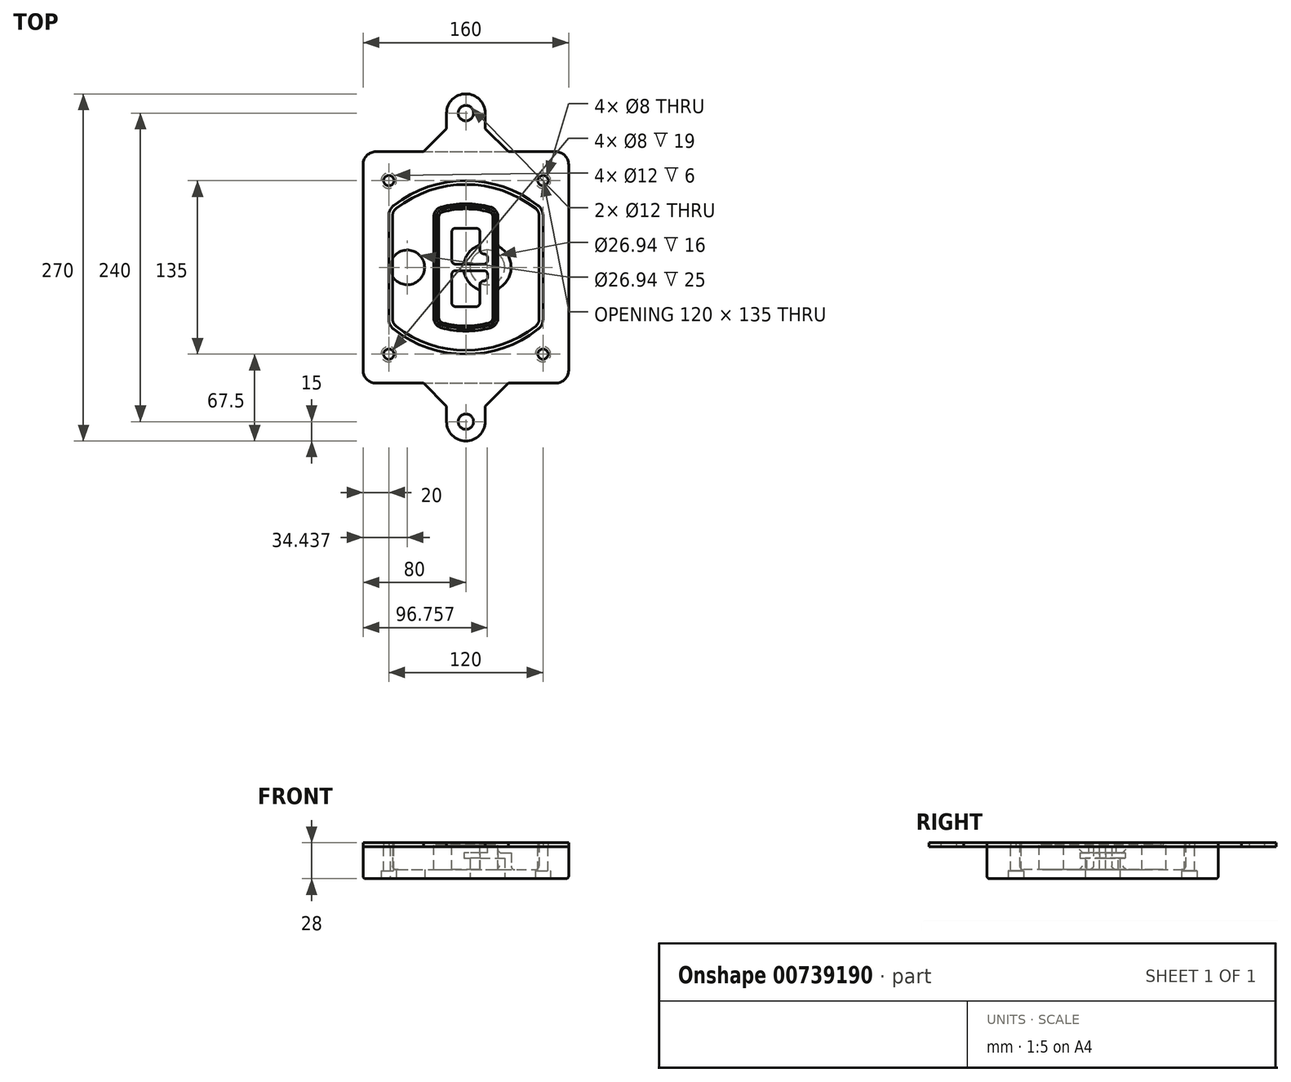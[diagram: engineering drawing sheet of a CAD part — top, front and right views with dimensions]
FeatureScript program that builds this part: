
annotation { "Feature Type Name" : "Feature", "Feature Type Description" : "" }
export const myFeature = defineFeature(function(context is Context, id is Id, definition is map)
    precondition{}
    {
        {
            var Q0;
            Q0=qCreatedBy(makeId("Top.planeOp"),FACE);
            var sketch = newSketch(context, id + "F0", { "sketchPlane" : qUnion([Q0])});
            skPoint(sketch, "E0.rect.middle", {"position": v(0, 0) * mm});
            skLineSegment(sketch, "E1.bottom", {"start": v(-70, -90) * mm, "end": v(70, -90) * mm});
            skLineSegment(sketch, "E1.top", {"start": v(-70, 90) * mm, "end": v(70, 90) * mm});
            skLineSegment(sketch, "E1.left", {"start": v(-80, -80) * mm, "end": v(-80, 80) * mm});
            skLineSegment(sketch, "E1.right", {"start": v(80, -80) * mm, "end": v(80, 80) * mm});
            skLineSegment(sketch, "E2", {"start": v(-80, 90) * mm, "end": v(80, -90) * mm, "construction": true});
            skLineSegment(sketch, "E3", {"start": v(80, 90) * mm, "end": v(-80, -90) * mm, "construction": true});
            skCircle(sketch, "E4", {"center": v(-60, 67.5) * mm, "radius": 4 * mm});
            skCircle(sketch, "E5", {"center": v(60, 67.5) * mm, "radius": 4 * mm});
            skCircle(sketch, "E6", {"center": v(60, -67.5) * mm, "radius": 4 * mm});
            skCircle(sketch, "E7", {"center": v(-60, -67.5) * mm, "radius": 4 * mm});
            skLineSegment(sketch, "E8", {"start": v(-60, 67.5) * mm, "end": v(60, 67.5) * mm, "construction": true});
            skLineSegment(sketch, "E9", {"start": v(60, 67.5) * mm, "end": v(60, -67.5) * mm, "construction": true});
            skLineSegment(sketch, "E10", {"start": v(60, -67.5) * mm, "end": v(-60, -67.5) * mm, "construction": true});
            skLineSegment(sketch, "E11", {"start": v(-60, -67.5) * mm, "end": v(-60, 67.5) * mm, "construction": true});
            skLineSegment(sketch, "E12", {"start": v(-60, 40.3) * mm, "end": v(-60, -40.3) * mm});
            skLineSegment(sketch, "E13", {"start": v(60, 40.3) * mm, "end": v(60, -40.3) * mm});
            skArc(sketch, "E14", {"start": v(56.15, 48.18) * mm, "mid": v(0, 67.5) * mm, "end": v(-56.15, 48.18) * mm});
            skArc(sketch, "E15", {"start": v(-56.15, -48.18) * mm, "mid": v(0, -67.5) * mm, "end": v(56.15, -48.18) * mm});
            skLineSegment(sketch, "E16", {"start": v(-60, 0) * mm, "end": v(60, 0) * mm, "construction": true});
            skPoint(sketch, "E17.visualSharp", {"position": v(-60, -45) * mm});
            skArc(sketch, "E17.filletArc", {"start": v(-60, -40.3) * mm, "mid": v(-58.99, -44.68) * mm, "end": v(-56.15, -48.18) * mm});
            skPoint(sketch, "E18.visualSharp", {"position": v(-60, 45) * mm});
            skArc(sketch, "E18.filletArc", {"start": v(-56.15, 48.18) * mm, "mid": v(-58.99, 44.68) * mm, "end": v(-60, 40.3) * mm});
            skPoint(sketch, "E19.visualSharp", {"position": v(60, 45) * mm});
            skArc(sketch, "E19.filletArc", {"start": v(60, 40.3) * mm, "mid": v(58.99, 44.68) * mm, "end": v(56.15, 48.18) * mm});
            skPoint(sketch, "E20.visualSharp", {"position": v(60, -45) * mm});
            skArc(sketch, "E20.filletArc", {"start": v(56.15, -48.18) * mm, "mid": v(58.99, -44.68) * mm, "end": v(60, -40.3) * mm});
            skPoint(sketch, "E21.visualSharp", {"position": v(-80, 90) * mm});
            skArc(sketch, "E21.filletArc", {"start": v(-70, 90) * mm, "mid": v(-77.07, 87.07) * mm, "end": v(-80, 80) * mm});
            skPoint(sketch, "E22.visualSharp", {"position": v(80, 90) * mm});
            skArc(sketch, "E22.filletArc", {"start": v(80, 80) * mm, "mid": v(77.07, 87.07) * mm, "end": v(70, 90) * mm});
            skPoint(sketch, "E23.visualSharp", {"position": v(80, -90) * mm});
            skArc(sketch, "E23.filletArc", {"start": v(70, -90) * mm, "mid": v(77.07, -87.07) * mm, "end": v(80, -80) * mm});
            skPoint(sketch, "E24.visualSharp", {"position": v(-80, -90) * mm});
            skArc(sketch, "E24.filletArc", {"start": v(-80, -80) * mm, "mid": v(-77.07, -87.07) * mm, "end": v(-70, -90) * mm});
            skArc(sketch, "E25.0", {"start": v(57, 40.3) * mm, "mid": v(56.3, 43.36) * mm, "end": v(54.3, 45.81) * mm});
            skLineSegment(sketch, "E25.1", {"start": v(57, 40.3) * mm, "end": v(57, -40.3) * mm});
            skArc(sketch, "E25.2", {"start": v(54.3, -45.81) * mm, "mid": v(56.3, -43.36) * mm, "end": v(57, -40.3) * mm});
            skArc(sketch, "E25.3", {"start": v(-54.3, -45.81) * mm, "mid": v(0, -64.5) * mm, "end": v(54.3, -45.81) * mm});
            skArc(sketch, "E25.4", {"start": v(-57, -40.3) * mm, "mid": v(-56.3, -43.36) * mm, "end": v(-54.3, -45.81) * mm});
            skArc(sketch, "E25.5", {"start": v(54.3, 45.81) * mm, "mid": v(0, 64.5) * mm, "end": v(-54.3, 45.81) * mm});
            skLineSegment(sketch, "E25.6", {"start": v(-57, 40.3) * mm, "end": v(-57, -40.3) * mm});
            skArc(sketch, "E25.7", {"start": v(-54.3, 45.81) * mm, "mid": v(-56.3, 43.36) * mm, "end": v(-57, 40.3) * mm});
            skArc(sketch, "E26.0", {"start": v(-58.62, 51.33) * mm, "mid": v(-62.58, 46.43) * mm, "end": v(-64, 40.3) * mm});
            skArc(sketch, "E26.1", {"start": v(58.62, 51.33) * mm, "mid": v(0, 71.5) * mm, "end": v(-58.62, 51.33) * mm});
            skArc(sketch, "E26.2", {"start": v(64, 40.3) * mm, "mid": v(62.58, 46.43) * mm, "end": v(58.62, 51.33) * mm});
            skLineSegment(sketch, "E26.3", {"start": v(64, 40.3) * mm, "end": v(64, -40.3) * mm});
            skArc(sketch, "E26.4", {"start": v(58.62, -51.33) * mm, "mid": v(62.58, -46.43) * mm, "end": v(64, -40.3) * mm});
            skLineSegment(sketch, "E26.5", {"start": v(-64, 40.3) * mm, "end": v(-64, -40.3) * mm});
            skArc(sketch, "E26.6", {"start": v(-58.62, -51.33) * mm, "mid": v(0, -71.5) * mm, "end": v(58.62, -51.33) * mm});
            skArc(sketch, "E26.7", {"start": v(-64, -40.3) * mm, "mid": v(-62.58, -46.43) * mm, "end": v(-58.62, -51.33) * mm});
            skSolve(sketch);
        }
        {
            var Q0;
            Q0=makeQuery(id+"F0.imprint","IMPRINT",FACE,{"disambiguationData":[TD([[makeQuery(id+"F0.imprint","IMPRINT",EDGE,{"derivedFrom":sQuery(id+"F0.wireOp",EDGE,"E1.bottom")}),1.0]])]});
            var Q1;
            Q1=makeQuery(id+"F0.imprint","IMPRINT",FACE,{"disambiguationData":[TD([[makeQuery(id+"F0.imprint","IMPRINT",EDGE,{"derivedFrom":sQuery(id+"F0.wireOp",EDGE,"E12")}),1.0]])]});
            var Q2;
            Q2=makeQuery(id+"F0.imprint","IMPRINT",FACE,{"disambiguationData":[TD([[makeQuery(id+"F0.imprint","IMPRINT",EDGE,{"derivedFrom":sQuery(id+"F0.wireOp",EDGE,"E25.0")}),1.0]])]});
            var Q3;
            Q3=makeQuery(id+"F0.imprint","IMPRINT",FACE,{"disambiguationData":[TD([[makeQuery(id+"F0.imprint","IMPRINT",EDGE,{"derivedFrom":sQuery(id+"F0.wireOp",EDGE,"E12")}),-1.0]])]});
            extrude(context, id + "F1", {"entities" : qUnion([Q0, Q1, Q2, Q3]), "oppositeDirection" : true, "depth" : 25 * mm});
        }
        {
            var Q0;
            Q0=makeQuery(id+"F0.imprint","IMPRINT",FACE,{"disambiguationData":[TD([[makeQuery(id+"F0.imprint","IMPRINT",EDGE,{"derivedFrom":sQuery(id+"F0.wireOp",EDGE,"E12")}),1.0]])]});
            extrude(context, id + "F2", {"entities" : qUnion([Q0]), "operationType" : NewBodyOperationType.ADD, "depth" : 3 * mm});
        }
        {
            var Q0;
            Q0=makeQuery(id+"F0.imprint","IMPRINT",FACE,{"disambiguationData":[TD([[makeQuery(id+"F0.imprint","IMPRINT",EDGE,{"derivedFrom":sQuery(id+"F0.wireOp",EDGE,"E25.0")}),1.0]])]});
            extrude(context, id + "F3", {"entities" : qUnion([Q0]), "operationType" : NewBodyOperationType.REMOVE, "oppositeDirection" : true, "depth" : 18 * mm});
        }
        {
            var Q0;
            Q0=makeQuery(id+"F2.opExtrude","CAP_FACE",FACE,{"disambiguationData":[OSD([sQuery(id+"F0.wireOp",EDGE,"E12"),sQuery(id+"F0.wireOp",EDGE,"E13"),sQuery(id+"F0.wireOp",EDGE,"E14"),sQuery(id+"F0.wireOp",EDGE,"E15"),sQuery(id+"F0.wireOp",EDGE,"E17.filletArc"),sQuery(id+"F0.wireOp",EDGE,"E18.filletArc"),sQuery(id+"F0.wireOp",EDGE,"E19.filletArc"),sQuery(id+"F0.wireOp",EDGE,"E20.filletArc"),sQuery(id+"F0.wireOp",EDGE,"E25.0"),sQuery(id+"F0.wireOp",EDGE,"E25.1"),sQuery(id+"F0.wireOp",EDGE,"E25.2"),sQuery(id+"F0.wireOp",EDGE,"E25.3"),sQuery(id+"F0.wireOp",EDGE,"E25.4"),sQuery(id+"F0.wireOp",EDGE,"E25.5"),sQuery(id+"F0.wireOp",EDGE,"E25.6"),sQuery(id+"F0.wireOp",EDGE,"E25.7")])],"isStart":false});
            var sketch = newSketch(context, id + "F4", { "sketchPlane" : qUnion([Q0])});
            skArc(sketch, "E27.0", {"start": v(-19.08, -46.97) * mm, "mid": v(0, -49.5) * mm, "end": v(19.08, -46.97) * mm});
            skArc(sketch, "E28.0", {"start": v(19.08, 46.97) * mm, "mid": v(0, 49.5) * mm, "end": v(-19.08, 46.97) * mm});
            skLineSegment(sketch, "E29", {"start": v(-25, 39.25) * mm, "end": v(-25, -39.25) * mm});
            skLineSegment(sketch, "E30", {"start": v(25, 39.25) * mm, "end": v(25, -39.25) * mm});
            skLineSegment(sketch, "E31", {"start": v(-25, 45.1) * mm, "end": v(25, 45.1) * mm, "construction": true});
            skLineSegment(sketch, "E32", {"start": v(-25, -45.1) * mm, "end": v(25, -45.1) * mm, "construction": true});
            skPoint(sketch, "E33.visualSharp", {"position": v(-25, 45.1) * mm});
            skArc(sketch, "E33.filletArc", {"start": v(-19.08, 46.97) * mm, "mid": v(-23.35, 44.11) * mm, "end": v(-25, 39.25) * mm});
            skPoint(sketch, "E34.visualSharp", {"position": v(25, 45.1) * mm});
            skArc(sketch, "E34.filletArc", {"start": v(25, 39.25) * mm, "mid": v(23.35, 44.11) * mm, "end": v(19.08, 46.97) * mm});
            skPoint(sketch, "E35.visualSharp", {"position": v(25, -45.1) * mm});
            skArc(sketch, "E35.filletArc", {"start": v(19.08, -46.97) * mm, "mid": v(23.35, -44.11) * mm, "end": v(25, -39.25) * mm});
            skPoint(sketch, "E36.visualSharp", {"position": v(-25, -45.1) * mm});
            skArc(sketch, "E36.filletArc", {"start": v(-25, -39.25) * mm, "mid": v(-23.35, -44.11) * mm, "end": v(-19.08, -46.97) * mm});
            skArc(sketch, "E37.0", {"start": v(54.3, 45.81) * mm, "mid": v(0, 64.5) * mm, "end": v(-54.3, 45.81) * mm});
            skArc(sketch, "E37.1", {"start": v(-54.3, 45.81) * mm, "mid": v(-56.3, 43.36) * mm, "end": v(-57, 40.3) * mm});
            skLineSegment(sketch, "E37.2", {"start": v(-57, 40.3) * mm, "end": v(-57, -40.3) * mm});
            skArc(sketch, "E37.3", {"start": v(-57, -40.3) * mm, "mid": v(-56.3, -43.36) * mm, "end": v(-54.3, -45.81) * mm});
            skArc(sketch, "E37.4", {"start": v(-54.3, -45.81) * mm, "mid": v(0, -64.5) * mm, "end": v(54.3, -45.81) * mm});
            skArc(sketch, "E37.5", {"start": v(54.3, -45.81) * mm, "mid": v(56.3, -43.36) * mm, "end": v(57, -40.3) * mm});
            skLineSegment(sketch, "E37.6", {"start": v(57, 40.3) * mm, "end": v(57, -40.3) * mm});
            skArc(sketch, "E37.7", {"start": v(57, 40.3) * mm, "mid": v(56.3, 43.36) * mm, "end": v(54.3, 45.81) * mm});
            skLineSegment(sketch, "E38.0", {"start": v(23, 39.25) * mm, "end": v(23, -39.25) * mm});
            skArc(sketch, "E38.1", {"start": v(18.56, -45.04) * mm, "mid": v(21.76, -42.9) * mm, "end": v(23, -39.25) * mm});
            skArc(sketch, "E38.2", {"start": v(-18.56, -45.04) * mm, "mid": v(0, -47.5) * mm, "end": v(18.56, -45.04) * mm});
            skArc(sketch, "E38.3", {"start": v(-23, -39.25) * mm, "mid": v(-21.76, -42.9) * mm, "end": v(-18.56, -45.04) * mm});
            skLineSegment(sketch, "E38.4", {"start": v(-23, 39.25) * mm, "end": v(-23, -39.25) * mm});
            skArc(sketch, "E38.5", {"start": v(23, 39.25) * mm, "mid": v(21.76, 42.9) * mm, "end": v(18.56, 45.04) * mm});
            skArc(sketch, "E38.6", {"start": v(-18.56, 45.04) * mm, "mid": v(-21.76, 42.9) * mm, "end": v(-23, 39.25) * mm});
            skArc(sketch, "E38.7", {"start": v(18.56, 45.04) * mm, "mid": v(0, 47.5) * mm, "end": v(-18.56, 45.04) * mm});
            skArc(sketch, "E39.0", {"start": v(21, 39.25) * mm, "mid": v(20.18, 41.68) * mm, "end": v(18.04, 43.1) * mm});
            skLineSegment(sketch, "E39.1", {"start": v(21, 39.25) * mm, "end": v(21, -39.25) * mm});
            skArc(sketch, "E39.2", {"start": v(18.04, -43.1) * mm, "mid": v(20.18, -41.68) * mm, "end": v(21, -39.25) * mm});
            skArc(sketch, "E39.3", {"start": v(-18.04, -43.1) * mm, "mid": v(0, -45.5) * mm, "end": v(18.04, -43.1) * mm});
            skArc(sketch, "E39.4", {"start": v(-21, -39.25) * mm, "mid": v(-20.18, -41.68) * mm, "end": v(-18.04, -43.1) * mm});
            skArc(sketch, "E39.5", {"start": v(18.04, 43.1) * mm, "mid": v(0, 45.5) * mm, "end": v(-18.04, 43.1) * mm});
            skLineSegment(sketch, "E39.6", {"start": v(-21, 39.25) * mm, "end": v(-21, -39.25) * mm});
            skArc(sketch, "E39.7", {"start": v(-18.04, 43.1) * mm, "mid": v(-20.18, 41.68) * mm, "end": v(-21, 39.25) * mm});
            skLineSegment(sketch, "E40", {"start": v(-25, 0) * mm, "end": v(25, 0) * mm, "construction": true});
            skLineSegment(sketch, "E41", {"start": v(-11, 5.5) * mm, "end": v(-11, 27.5) * mm});
            skLineSegment(sketch, "E42", {"start": v(-8, 30.5) * mm, "end": v(8, 30.5) * mm});
            skLineSegment(sketch, "E43", {"start": v(11, 27.5) * mm, "end": v(11, 13.5) * mm});
            skLineSegment(sketch, "E44", {"start": v(14, 10.5) * mm, "end": v(14, 10.5) * mm});
            skLineSegment(sketch, "E45", {"start": v(17, 7.5) * mm, "end": v(17, 5.5) * mm});
            skLineSegment(sketch, "E46", {"start": v(14, 2.5) * mm, "end": v(-8, 2.5) * mm});
            skPoint(sketch, "E47.visualSharp", {"position": v(-11, 30.5) * mm});
            skArc(sketch, "E47.filletArc", {"start": v(-8, 30.5) * mm, "mid": v(-10.12, 29.62) * mm, "end": v(-11, 27.5) * mm});
            skPoint(sketch, "E48.visualSharp", {"position": v(11, 30.5) * mm});
            skArc(sketch, "E48.filletArc", {"start": v(11, 27.5) * mm, "mid": v(10.12, 29.62) * mm, "end": v(8, 30.5) * mm});
            skPoint(sketch, "E49.visualSharp", {"position": v(11, 10.5) * mm});
            skArc(sketch, "E49.filletArc", {"start": v(11, 13.5) * mm, "mid": v(11.88, 11.38) * mm, "end": v(14, 10.5) * mm});
            skPoint(sketch, "E50.visualSharp", {"position": v(17, 10.5) * mm});
            skArc(sketch, "E50.filletArc", {"start": v(17, 7.5) * mm, "mid": v(16.12, 9.62) * mm, "end": v(14, 10.5) * mm});
            skPoint(sketch, "E51.visualSharp", {"position": v(17, 2.5) * mm});
            skArc(sketch, "E51.filletArc", {"start": v(14, 2.5) * mm, "mid": v(16.12, 3.38) * mm, "end": v(17, 5.5) * mm});
            skPoint(sketch, "E52.visualSharp", {"position": v(-11, 2.5) * mm});
            skArc(sketch, "E52.filletArc", {"start": v(-11, 5.5) * mm, "mid": v(-10.12, 3.38) * mm, "end": v(-8, 2.5) * mm});
            skLineSegment(sketch, "E53.0.MirrorCS", {"start": v(14, -2.5) * mm, "end": v(-8, -2.5) * mm});
            skArc(sketch, "E54.0.MirrorCS", {"start": v(-11, -5.5) * mm, "mid": v(-10.12, -3.38) * mm, "end": v(-8, -2.5) * mm});
            skLineSegment(sketch, "E55.0.MirrorCS", {"start": v(-11, -5.5) * mm, "end": v(-11, -27.5) * mm});
            skArc(sketch, "E56.0.MirrorCS", {"start": v(-8, -30.5) * mm, "mid": v(-10.12, -29.62) * mm, "end": v(-11, -27.5) * mm});
            skLineSegment(sketch, "E57.0.MirrorCS", {"start": v(-8, -30.5) * mm, "end": v(8, -30.5) * mm});
            skArc(sketch, "E58.0.MirrorCS", {"start": v(11, -27.5) * mm, "mid": v(10.12, -29.62) * mm, "end": v(8, -30.5) * mm});
            skLineSegment(sketch, "E59.0.MirrorCS", {"start": v(11, -27.5) * mm, "end": v(11, -13.5) * mm});
            skArc(sketch, "E60.0.MirrorCS", {"start": v(11, -13.5) * mm, "mid": v(11.88, -11.38) * mm, "end": v(14, -10.5) * mm});
            skArc(sketch, "E61.0.MirrorCS", {"start": v(17, -7.5) * mm, "mid": v(16.12, -9.62) * mm, "end": v(14, -10.5) * mm});
            skLineSegment(sketch, "E62.0.MirrorCS", {"start": v(17, -7.5) * mm, "end": v(17, -5.5) * mm});
            skArc(sketch, "E63.0.MirrorCS", {"start": v(14, -2.5) * mm, "mid": v(16.12, -3.38) * mm, "end": v(17, -5.5) * mm});
            skSolve(sketch);
        }
        {
            var Q0;
            Q0=makeQuery(id+"F4.imprint","IMPRINT",FACE,{"disambiguationData":[TD([[makeQuery(id+"F4.imprint","IMPRINT",EDGE,{"derivedFrom":sQuery(id+"F4.wireOp",EDGE,"E27.0")}),1.0]])]});
            var Q1;
            Q1=makeQuery(id+"F4.imprint","IMPRINT",FACE,{"disambiguationData":[TD([[makeQuery(id+"F4.imprint","IMPRINT",EDGE,{"derivedFrom":sQuery(id+"F4.wireOp",EDGE,"E38.0")}),-1.0]])]});
            var Q2;
            Q2=makeQuery(id+"F4.imprint","IMPRINT",FACE,{"disambiguationData":[TD([[makeQuery(id+"F4.imprint","IMPRINT",EDGE,{"derivedFrom":sQuery(id+"F4.wireOp",EDGE,"E39.0")}),1.0]])]});
            extrude(context, id + "F5", {"entities" : qUnion([Q0, Q1, Q2]), "operationType" : NewBodyOperationType.ADD, "endBound" : BoundingType.UP_TO_NEXT, "oppositeDirection" : true, "depth" : 25 * mm});
        }
        {
            var Q0;
            Q0=makeQuery(id+"F4.imprint","IMPRINT",FACE,{"disambiguationData":[TD([[makeQuery(id+"F4.imprint","IMPRINT",EDGE,{"derivedFrom":sQuery(id+"F4.wireOp",EDGE,"E38.0")}),-1.0]])]});
            extrude(context, id + "F6", {"entities" : qUnion([Q0]), "operationType" : NewBodyOperationType.REMOVE, "oppositeDirection" : true, "depth" : 2 * mm});
        }
        {
            var Q0;
            Q0=makeQuery(id+"F1.opExtrude","CAP_FACE",FACE,{"disambiguationData":[OSD([sQuery(id+"F0.wireOp",EDGE,"E1.bottom"),sQuery(id+"F0.wireOp",EDGE,"E1.top"),sQuery(id+"F0.wireOp",EDGE,"E1.left"),sQuery(id+"F0.wireOp",EDGE,"E1.right"),sQuery(id+"F0.wireOp",EDGE,"E4"),sQuery(id+"F0.wireOp",EDGE,"E5"),sQuery(id+"F0.wireOp",EDGE,"E6"),sQuery(id+"F0.wireOp",EDGE,"E7"),sQuery(id+"F0.wireOp",EDGE,"E21.filletArc"),sQuery(id+"F0.wireOp",EDGE,"E22.filletArc"),sQuery(id+"F0.wireOp",EDGE,"E23.filletArc"),sQuery(id+"F0.wireOp",EDGE,"E24.filletArc")])],"isStart":false});
            var sketch = newSketch(context, id + "F7", { "sketchPlane" : qUnion([Q0])});
            skCircle(sketch, "E64", {"center": v(16.76, 0) * mm, "radius": 13.47 * mm});
            skCircle(sketch, "E65", {"center": v(-45.56, 0) * mm, "radius": 13.47 * mm});
            skLineSegment(sketch, "E66", {"start": v(80, 0) * mm, "end": v(-80, 0) * mm});
            skCircle(sketch, "E67", {"center": v(16.76, 0) * mm, "radius": 18.47 * mm});
            skCircle(sketch, "E68", {"center": v(60, -67.5) * mm, "radius": 6 * mm});
            skCircle(sketch, "E69", {"center": v(-60, -67.5) * mm, "radius": 6 * mm});
            skCircle(sketch, "E70", {"center": v(-60, 67.5) * mm, "radius": 6 * mm});
            skCircle(sketch, "E71", {"center": v(60, 67.5) * mm, "radius": 6 * mm});
            skSolve(sketch);
        }
        {
            var Q0;
            {var subQ1=sQuery(id+"F7.wireOp",EDGE,"E66");var subQ4=sQuery(id+"F7.wireOp",EDGE,"E64");var subQ6=makeQuery(id+"F7.imprint","INTERSECT",VERTEX,{"disambiguationData":[OD(0.0)],"derivedFrom":[subQ4,subQ1]});Q0=makeQuery(id+"F7.imprint","IMPRINT",FACE,{"disambiguationData":[TD([[makeQuery(id+"F7.imprint","IMPRINT",EDGE,{"disambiguationData":[TD([[subQ6,-1.0]])],"derivedFrom":subQ4}),-1.0]])]});}
            var Q1;
            {var subQ0=sQuery(id+"F7.wireOp",EDGE,"E66");var subQ1=sQuery(id+"F7.wireOp",EDGE,"E64");var subQ3=makeQuery(id+"F7.imprint","INTERSECT",VERTEX,{"disambiguationData":[OD(0.0)],"derivedFrom":[subQ1,subQ0]});Q1=makeQuery(id+"F7.imprint","IMPRINT",FACE,{"disambiguationData":[TD([[makeQuery(id+"F7.imprint","IMPRINT",EDGE,{"disambiguationData":[TD([[subQ3,-1.0]])],"derivedFrom":subQ1}),1.0]])]});}
            var Q2;
            {var subQ0=sQuery(id+"F7.wireOp",EDGE,"E66");var subQ1=sQuery(id+"F7.wireOp",EDGE,"E64");var subQ3=makeQuery(id+"F7.imprint","INTERSECT",VERTEX,{"disambiguationData":[OD(0.0)],"derivedFrom":[subQ1,subQ0]});Q2=makeQuery(id+"F7.imprint","IMPRINT",FACE,{"disambiguationData":[TD([[makeQuery(id+"F7.imprint","IMPRINT",EDGE,{"disambiguationData":[TD([[subQ3,1.0]])],"derivedFrom":subQ1}),1.0]])]});}
            var Q3;
            {var subQ1=sQuery(id+"F7.wireOp",EDGE,"E66");var subQ4=sQuery(id+"F7.wireOp",EDGE,"E64");var subQ6=makeQuery(id+"F7.imprint","INTERSECT",VERTEX,{"disambiguationData":[OD(0.0)],"derivedFrom":[subQ4,subQ1]});Q3=makeQuery(id+"F7.imprint","IMPRINT",FACE,{"disambiguationData":[TD([[makeQuery(id+"F7.imprint","IMPRINT",EDGE,{"disambiguationData":[TD([[subQ6,1.0]])],"derivedFrom":subQ4}),-1.0]])]});}
            extrude(context, id + "F8", {"entities" : qUnion([Q0, Q1, Q2, Q3]), "operationType" : NewBodyOperationType.ADD, "oppositeDirection" : true, "depth" : 20 * mm});
        }
        {
            var Q0;
            {var subQ0=sQuery(id+"F7.wireOp",EDGE,"E66");var subQ1=sQuery(id+"F7.wireOp",EDGE,"E64");var subQ3=makeQuery(id+"F7.imprint","INTERSECT",VERTEX,{"disambiguationData":[OD(0.0)],"derivedFrom":[subQ1,subQ0]});Q0=makeQuery(id+"F7.imprint","IMPRINT",FACE,{"disambiguationData":[TD([[makeQuery(id+"F7.imprint","IMPRINT",EDGE,{"disambiguationData":[TD([[subQ3,-1.0]])],"derivedFrom":subQ1}),1.0]])]});}
            var Q1;
            {var subQ0=sQuery(id+"F7.wireOp",EDGE,"E66");var subQ1=sQuery(id+"F7.wireOp",EDGE,"E64");var subQ3=makeQuery(id+"F7.imprint","INTERSECT",VERTEX,{"disambiguationData":[OD(0.0)],"derivedFrom":[subQ1,subQ0]});Q1=makeQuery(id+"F7.imprint","IMPRINT",FACE,{"disambiguationData":[TD([[makeQuery(id+"F7.imprint","IMPRINT",EDGE,{"disambiguationData":[TD([[subQ3,1.0]])],"derivedFrom":subQ1}),1.0]])]});}
            extrude(context, id + "F9", {"entities" : qUnion([Q0, Q1]), "operationType" : NewBodyOperationType.REMOVE, "oppositeDirection" : true, "depth" : 16 * mm});
        }
        {
            var Q0;
            {var subQ0=sQuery(id+"F7.wireOp",EDGE,"E66");var subQ1=sQuery(id+"F7.wireOp",EDGE,"E65");var subQ3=makeQuery(id+"F7.imprint","INTERSECT",VERTEX,{"disambiguationData":[OD(0.0)],"derivedFrom":[subQ1,subQ0]});Q0=makeQuery(id+"F7.imprint","IMPRINT",FACE,{"disambiguationData":[TD([[makeQuery(id+"F7.imprint","IMPRINT",EDGE,{"disambiguationData":[TD([[subQ3,-1.0]])],"derivedFrom":subQ1}),1.0]])]});}
            var Q1;
            {var subQ0=sQuery(id+"F7.wireOp",EDGE,"E66");var subQ1=sQuery(id+"F7.wireOp",EDGE,"E65");var subQ3=makeQuery(id+"F7.imprint","INTERSECT",VERTEX,{"disambiguationData":[OD(0.0)],"derivedFrom":[subQ1,subQ0]});Q1=makeQuery(id+"F7.imprint","IMPRINT",FACE,{"disambiguationData":[TD([[makeQuery(id+"F7.imprint","IMPRINT",EDGE,{"disambiguationData":[TD([[subQ3,1.0]])],"derivedFrom":subQ1}),1.0]])]});}
            extrude(context, id + "F10", {"entities" : qUnion([Q0, Q1]), "operationType" : NewBodyOperationType.REMOVE, "oppositeDirection" : true, "depth" : 25 * mm});
        }
        {
            var Q0;
            Q0=makeQuery(id+"F7.imprint","IMPRINT",FACE,{"disambiguationData":[TD([[makeQuery(id+"F7.imprint","IMPRINT",EDGE,{"derivedFrom":sQuery(id+"F7.wireOp",EDGE,"E68")}),1.0]])]});
            var Q1;
            Q1=makeQuery(id+"F7.imprint","IMPRINT",FACE,{"disambiguationData":[TD([[makeQuery(id+"F7.imprint","IMPRINT",EDGE,{"derivedFrom":makeQuery(id+"F1.opExtrude","CAP_EDGE",EDGE,{"disambiguationData":[OSD([sQuery(id+"F0.wireOp",EDGE,"E5")])],"isStart":false})}),-1.0]])]});
            var Q2;
            Q2=makeQuery(id+"F7.imprint","IMPRINT",FACE,{"disambiguationData":[TD([[makeQuery(id+"F7.imprint","IMPRINT",EDGE,{"derivedFrom":sQuery(id+"F7.wireOp",EDGE,"E69")}),1.0]])]});
            var Q3;
            Q3=makeQuery(id+"F7.imprint","IMPRINT",FACE,{"disambiguationData":[TD([[makeQuery(id+"F7.imprint","IMPRINT",EDGE,{"derivedFrom":makeQuery(id+"F1.opExtrude","CAP_EDGE",EDGE,{"disambiguationData":[OSD([sQuery(id+"F0.wireOp",EDGE,"E4")])],"isStart":false})}),-1.0]])]});
            var Q4;
            Q4=makeQuery(id+"F7.imprint","IMPRINT",FACE,{"disambiguationData":[TD([[makeQuery(id+"F7.imprint","IMPRINT",EDGE,{"derivedFrom":sQuery(id+"F7.wireOp",EDGE,"E70")}),1.0]])]});
            var Q5;
            Q5=makeQuery(id+"F7.imprint","IMPRINT",FACE,{"disambiguationData":[TD([[makeQuery(id+"F7.imprint","IMPRINT",EDGE,{"derivedFrom":makeQuery(id+"F1.opExtrude","CAP_EDGE",EDGE,{"disambiguationData":[OSD([sQuery(id+"F0.wireOp",EDGE,"E7")])],"isStart":false})}),-1.0]])]});
            var Q6;
            Q6=makeQuery(id+"F7.imprint","IMPRINT",FACE,{"disambiguationData":[TD([[makeQuery(id+"F7.imprint","IMPRINT",EDGE,{"derivedFrom":sQuery(id+"F7.wireOp",EDGE,"E71")}),1.0]])]});
            var Q7;
            Q7=makeQuery(id+"F7.imprint","IMPRINT",FACE,{"disambiguationData":[TD([[makeQuery(id+"F7.imprint","IMPRINT",EDGE,{"derivedFrom":makeQuery(id+"F1.opExtrude","CAP_EDGE",EDGE,{"disambiguationData":[OSD([sQuery(id+"F0.wireOp",EDGE,"E6")])],"isStart":false})}),-1.0]])]});
            extrude(context, id + "F11", {"entities" : qUnion([Q0, Q1, Q2, Q3, Q4, Q5, Q6, Q7]), "operationType" : NewBodyOperationType.REMOVE, "oppositeDirection" : true, "depth" : 6 * mm});
        }
        {
            var Q0;
            Q0=makeQuery(id+"F9.boolean.opBoolean","COPY",FACE,{"derivedFrom":makeQuery(id+"F9.opExtrude","CAP_FACE",FACE,{"disambiguationData":[OSD([sQuery(id+"F7.wireOp",EDGE,"E64")])],"isStart":false})});
            var sketch = newSketch(context, id + "F12", { "sketchPlane" : qUnion([Q0])});
            skArc(sketch, "E72.0", {"start": v(11, 17.55) * mm, "mid": v(2.57, 11.82) * mm, "end": v(-1.54, 2.5) * mm});
            skArc(sketch, "E72.1", {"start": v(-1.54, -2.5) * mm, "mid": v(2.57, -11.82) * mm, "end": v(11, -17.55) * mm});
            skLineSegment(sketch, "E73", {"start": v(-1.54, -2.5) * mm, "end": v(14, -2.5) * mm});
            skLineSegment(sketch, "E74.0", {"start": v(14, 2.5) * mm, "end": v(-1.54, 2.5) * mm});
            skArc(sketch, "E74.1", {"start": v(14, 2.5) * mm, "mid": v(16.12, 3.38) * mm, "end": v(17, 5.5) * mm});
            skLineSegment(sketch, "E74.2", {"start": v(17, 7.5) * mm, "end": v(17, 5.5) * mm});
            skArc(sketch, "E74.3", {"start": v(17, 7.5) * mm, "mid": v(16.12, 9.62) * mm, "end": v(14, 10.5) * mm});
            skArc(sketch, "E74.4", {"start": v(11, 13.5) * mm, "mid": v(11.88, 11.38) * mm, "end": v(14, 10.5) * mm});
            skLineSegment(sketch, "E74.5", {"start": v(11, 17.55) * mm, "end": v(11, 13.5) * mm});
            skLineSegment(sketch, "E74.7", {"start": v(14, -2.5) * mm, "end": v(-1.54, -2.5) * mm});
            skArc(sketch, "E74.8", {"start": v(14, -2.5) * mm, "mid": v(16.12, -3.38) * mm, "end": v(17, -5.5) * mm});
            skLineSegment(sketch, "E74.9", {"start": v(17, -7.5) * mm, "end": v(17, -5.5) * mm});
            skArc(sketch, "E74.10", {"start": v(17, -7.5) * mm, "mid": v(16.12, -9.62) * mm, "end": v(14, -10.5) * mm});
            skArc(sketch, "E74.11", {"start": v(11, -13.5) * mm, "mid": v(11.88, -11.38) * mm, "end": v(14, -10.5) * mm});
            skLineSegment(sketch, "E74.12", {"start": v(11, -17.55) * mm, "end": v(11, -13.5) * mm});
            skPoint(sketch, "E75.orphan", {"position": v(11, -27.5) * mm});
            skPoint(sketch, "E76.orphan", {"position": v(-8, -2.5) * mm});
            skPoint(sketch, "E77.orphan", {"position": v(-8, 2.5) * mm});
            skPoint(sketch, "E78.orphan", {"position": v(11, 27.5) * mm});
            skSolve(sketch);
        }
        {
            var Q0;
            {var subQ7=sQuery(id+"F12.wireOp",EDGE,"E72.0");var subQ14=sQuery(id+"F12.wireOp",EDGE,"E72.1");var subQ16=sQuery(id+"F12.wireOp",EDGE,"E74.1");var subQ18=sQuery(id+"F12.wireOp",EDGE,"E74.8");Q0=qUnion([makeQuery(id+"F12.imprint","IMPRINT",FACE,{"disambiguationData":[TD([[makeQuery(id+"F12.imprint","IMPRINT",EDGE,{"derivedFrom":subQ7}),1.0]])]}),makeQuery(id+"F12.imprint","IMPRINT",FACE,{"disambiguationData":[TD([[makeQuery(id+"F12.imprint","IMPRINT",EDGE,{"derivedFrom":subQ14}),1.0]])]}),makeQuery(id+"F12.imprint","IMPRINT",FACE,{"disambiguationData":[TD([[makeQuery(id+"F12.imprint","IMPRINT",EDGE,{"derivedFrom":subQ16}),1.0]])]}),makeQuery(id+"F12.imprint","IMPRINT",FACE,{"disambiguationData":[TD([[makeQuery(id+"F12.imprint","IMPRINT",EDGE,{"derivedFrom":subQ18}),-1.0]])]})]);}
            var Q1;
            Q1=makeQuery(id+"F5.boolean.opBoolean","SPLIT",FACE,{"disambiguationData":[TD([makeQuery(id+"F5.opExtrude","SWEPT_FACE",FACE,{"disambiguationData":[OSD([sQuery(id+"F4.wireOp",EDGE,"E41")])]})])],"derivedFrom":makeQuery(id+"F3.boolean.opBoolean","COPY",FACE,{"derivedFrom":makeQuery(id+"F3.opExtrude","CAP_FACE",FACE,{"disambiguationData":[OSD([sQuery(id+"F0.wireOp",EDGE,"E25.0"),sQuery(id+"F0.wireOp",EDGE,"E25.1"),sQuery(id+"F0.wireOp",EDGE,"E25.2"),sQuery(id+"F0.wireOp",EDGE,"E25.3"),sQuery(id+"F0.wireOp",EDGE,"E25.4"),sQuery(id+"F0.wireOp",EDGE,"E25.5"),sQuery(id+"F0.wireOp",EDGE,"E25.6"),sQuery(id+"F0.wireOp",EDGE,"E25.7")])],"isStart":false})})});
            extrude(context, id + "F13", {"entities" : qUnion([Q0]), "operationType" : NewBodyOperationType.REMOVE, "endBound" : BoundingType.UP_TO_SURFACE, "endBoundEntityFace" : qUnion([Q1]), "depth" : 25 * mm});
        }
        {
            var Q0;
            Q0=makeQuery(id+"F3.boolean.opBoolean","COPY",EDGE,{"derivedFrom":makeQuery(id+"F3.opExtrude","CAP_EDGE",EDGE,{"disambiguationData":[OSD([sQuery(id+"F0.wireOp",EDGE,"E25.6")])],"isStart":false})});
            var Q1;
            Q1=makeQuery(id+"F8.boolean.opBoolean","INTERSECT",EDGE,{"derivedFrom":[makeQuery(id+"F5.opExtrude","SWEPT_FACE",FACE,{"disambiguationData":[OSD([sQuery(id+"F4.wireOp",EDGE,"E30")])]}),makeQuery(id+"F8.opExtrude","CAP_FACE",FACE,{"disambiguationData":[OSD([sQuery(id+"F7.wireOp",EDGE,"E67")])],"isStart":false})]});
            var Q2;
            Q2=makeQuery(id+"F8.boolean.opBoolean","INTERSECT",EDGE,{"disambiguationData":[OD(1.0)],"derivedFrom":[makeQuery(id+"F5.opExtrude","SWEPT_FACE",FACE,{"disambiguationData":[OSD([sQuery(id+"F4.wireOp",EDGE,"E30")])]}),makeQuery(id+"F8.opExtrude","SWEPT_FACE",FACE,{"disambiguationData":[OSD([sQuery(id+"F7.wireOp",EDGE,"E67")])]})]});
            var Q3;
            {var subQ0=makeQuery(id+"F3.boolean.opBoolean","COPY",FACE,{"derivedFrom":makeQuery(id+"F3.opExtrude","CAP_FACE",FACE,{"disambiguationData":[OSD([sQuery(id+"F0.wireOp",EDGE,"E25.0"),sQuery(id+"F0.wireOp",EDGE,"E25.1"),sQuery(id+"F0.wireOp",EDGE,"E25.2"),sQuery(id+"F0.wireOp",EDGE,"E25.3"),sQuery(id+"F0.wireOp",EDGE,"E25.4"),sQuery(id+"F0.wireOp",EDGE,"E25.5"),sQuery(id+"F0.wireOp",EDGE,"E25.6"),sQuery(id+"F0.wireOp",EDGE,"E25.7")])],"isStart":false})});var subQ1=sQuery(id+"F4.wireOp",EDGE,"E30");Q3=makeQuery(id+"F8.boolean.opBoolean","SPLIT",EDGE,{"disambiguationData":[TD([makeQuery(id+"F5.opExtrude","SWEPT_FACE",FACE,{"disambiguationData":[OSD([sQuery(id+"F4.wireOp",EDGE,"E35.filletArc")])]})])],"derivedFrom":makeQuery(id+"F5.opExtrude","TWEAK_EDGE",EDGE,{"derivedFrom":[subQ0,makeQuery(id+"F4.imprint","IMPRINT",EDGE,{"derivedFrom":subQ1})]})});}
            var Q4;
            {var subQ0=sQuery(id+"F0.wireOp",EDGE,"E25.0");var subQ1=sQuery(id+"F0.wireOp",EDGE,"E25.1");var subQ2=sQuery(id+"F0.wireOp",EDGE,"E25.2");var subQ3=sQuery(id+"F0.wireOp",EDGE,"E25.3");var subQ4=sQuery(id+"F0.wireOp",EDGE,"E25.4");var subQ5=sQuery(id+"F0.wireOp",EDGE,"E25.5");var subQ6=sQuery(id+"F0.wireOp",EDGE,"E25.6");var subQ7=sQuery(id+"F0.wireOp",EDGE,"E25.7");Q4=makeQuery(id+"F8.boolean.opBoolean","INTERSECT",EDGE,{"derivedFrom":[makeQuery(id+"F5.boolean.opBoolean","SPLIT",FACE,{"disambiguationData":[TD([makeQuery(id+"F2.opExtrude","SWEPT_FACE",FACE,{"disambiguationData":[OSD([subQ0])]})])],"derivedFrom":makeQuery(id+"F3.boolean.opBoolean","COPY",FACE,{"derivedFrom":makeQuery(id+"F3.opExtrude","CAP_FACE",FACE,{"disambiguationData":[OSD([subQ0,subQ1,subQ2,subQ3,subQ4,subQ5,subQ6,subQ7])],"isStart":false})})}),makeQuery(id+"F8.opExtrude","SWEPT_FACE",FACE,{"disambiguationData":[OSD([sQuery(id+"F7.wireOp",EDGE,"E67")])]})]});}
            var Q5;
            Q5=makeQuery(id+"F8.boolean.opBoolean","INTERSECT",EDGE,{"disambiguationData":[OD(0.0)],"derivedFrom":[makeQuery(id+"F5.opExtrude","SWEPT_FACE",FACE,{"disambiguationData":[OSD([sQuery(id+"F4.wireOp",EDGE,"E30")])]}),makeQuery(id+"F8.opExtrude","SWEPT_FACE",FACE,{"disambiguationData":[OSD([sQuery(id+"F7.wireOp",EDGE,"E67")])]})]});
            fillet(context, id + "F14", {"entities" : qUnion([Q0, Q1, Q2, Q3, Q4, Q5]), "radius" : 3 * mm, "tangentPropagation" : true, "allowEdgeOverflow" : false});
        }
        {
            var Q0;
            Q0=makeQuery(id+"F1.opExtrude","CAP_EDGE",EDGE,{"disambiguationData":[OSD([sQuery(id+"F0.wireOp",EDGE,"E1.bottom")])],"isStart":false});
            fillet(context, id + "F15", {"entities" : qUnion([Q0]), "radius" : 2 * mm, "tangentPropagation" : true, "allowEdgeOverflow" : false});
        }
        {
            var Q0;
            {var subQ0=sQuery(id+"F0.wireOp",EDGE,"E21.filletArc");var subQ1=sQuery(id+"F0.wireOp",EDGE,"E7");var subQ2=sQuery(id+"F0.wireOp",EDGE,"E6");var subQ3=sQuery(id+"F0.wireOp",EDGE,"E5");var subQ4=sQuery(id+"F0.wireOp",EDGE,"E4");var subQ5=sQuery(id+"F0.wireOp",EDGE,"E22.filletArc");var subQ6=sQuery(id+"F0.wireOp",EDGE,"E1.bottom");var subQ7=sQuery(id+"F0.wireOp",EDGE,"E1.right");var subQ8=sQuery(id+"F0.wireOp",EDGE,"E1.top");var subQ9=sQuery(id+"F0.wireOp",EDGE,"E1.left");var subQ10=sQuery(id+"F0.wireOp",EDGE,"E23.filletArc");var subQ11=sQuery(id+"F0.wireOp",EDGE,"E24.filletArc");Q0=makeQuery(id+"F2.boolean.opBoolean","SPLIT",FACE,{"disambiguationData":[TD([makeQuery(id+"F1.opExtrude","SWEPT_FACE",FACE,{"disambiguationData":[OSD([subQ6])]})])],"derivedFrom":makeQuery(id+"F1.opExtrude","CAP_FACE",FACE,{"disambiguationData":[OSD([subQ6,subQ8,subQ9,subQ7,subQ4,subQ3,subQ2,subQ1,subQ0,subQ5,subQ10,subQ11])],"isStart":true})});}
            var sketch = newSketch(context, id + "F16", { "sketchPlane" : qUnion([Q0])});
            skLineSegment(sketch, "E79", {"start": v(0, 90) * mm, "end": v(0, 120) * mm, "construction": true});
            skCircle(sketch, "E80", {"center": v(0, 120) * mm, "radius": 6 * mm});
            skArc(sketch, "E81", {"start": v(15, 120) * mm, "mid": v(0, 135) * mm, "end": v(-15, 120) * mm});
            skLineSegment(sketch, "E82", {"start": v(-15, 120) * mm, "end": v(-15, 108) * mm});
            skLineSegment(sketch, "E83", {"start": v(15, 120) * mm, "end": v(15, 108) * mm});
            skLineSegment(sketch, "E84", {"start": v(15, 108) * mm, "end": v(33, 90) * mm});
            skLineSegment(sketch, "E85", {"start": v(-15, 108) * mm, "end": v(-33, 90) * mm});
            skLineSegment(sketch, "E86", {"start": v(-80, 0) * mm, "end": v(80, 0) * mm, "construction": true});
            skLineSegment(sketch, "E87.MirrorCS", {"start": v(-15, -120) * mm, "end": v(-15, -108) * mm});
            skLineSegment(sketch, "E88.MirrorCS", {"start": v(15, -120) * mm, "end": v(15, -108) * mm});
            skLineSegment(sketch, "E89.MirrorCS", {"start": v(-15, -108) * mm, "end": v(-33, -90) * mm});
            skLineSegment(sketch, "E90.MirrorCS", {"start": v(15, -108) * mm, "end": v(33, -90) * mm});
            skArc(sketch, "E91.MirrorCS", {"start": v(15, -120) * mm, "mid": v(0, -135) * mm, "end": v(-15, -120) * mm});
            skCircle(sketch, "E92.MirrorC", {"center": v(0, -120) * mm, "radius": 6 * mm});
            skLineSegment(sketch, "E93.MirrorCS", {"start": v(0, -90) * mm, "end": v(0, -120) * mm, "construction": true});
            skLineSegment(sketch, "E94.0.0", {"start": v(70, 90) * mm, "end": v(-70, 90) * mm});
            skArc(sketch, "E94.0.1", {"start": v(-70, 90) * mm, "mid": v(-77.07, 87.07) * mm, "end": v(-80, 80) * mm});
            skLineSegment(sketch, "E94.0.2", {"start": v(-80, 80) * mm, "end": v(-80, -80) * mm});
            skArc(sketch, "E94.0.3", {"start": v(-80, -80) * mm, "mid": v(-77.07, -87.07) * mm, "end": v(-70, -90) * mm});
            skLineSegment(sketch, "E94.0.4", {"start": v(-70, -90) * mm, "end": v(70, -90) * mm});
            skArc(sketch, "E94.0.5", {"start": v(70, -90) * mm, "mid": v(77.07, -87.07) * mm, "end": v(80, -80) * mm});
            skLineSegment(sketch, "E94.0.6", {"start": v(80, -80) * mm, "end": v(80, 80) * mm});
            skArc(sketch, "E94.0.7", {"start": v(80, 80) * mm, "mid": v(77.07, 87.07) * mm, "end": v(70, 90) * mm});
            skSolve(sketch);
        }
        {
            var Q0;
            Q0=makeQuery(id+"F16.imprint","IMPRINT",FACE,{"disambiguationData":[TD([[makeQuery(id+"F16.imprint","IMPRINT",EDGE,{"derivedFrom":sQuery(id+"F16.wireOp",EDGE,"E87.MirrorCS")}),-1.0]])]});
            var Q1;
            {var subQ1=sQuery(id+"F16.wireOp",EDGE,"E94.0.1");Q1=makeQuery(id+"F16.imprint","IMPRINT",FACE,{"disambiguationData":[TD([[makeQuery(id+"F16.imprint","IMPRINT",EDGE,{"derivedFrom":subQ1}),1.0]])]});}
            var Q2;
            Q2=makeQuery(id+"F16.imprint","IMPRINT",FACE,{"disambiguationData":[TD([[makeQuery(id+"F16.imprint","IMPRINT",EDGE,{"derivedFrom":sQuery(id+"F16.wireOp",EDGE,"E80")}),-1.0]])]});
            var Q3;
            Q3=makeQuery(id+"F2.opExtrude","CAP_FACE",FACE,{"disambiguationData":[OSD([sQuery(id+"F0.wireOp",EDGE,"E12"),sQuery(id+"F0.wireOp",EDGE,"E13"),sQuery(id+"F0.wireOp",EDGE,"E14"),sQuery(id+"F0.wireOp",EDGE,"E15"),sQuery(id+"F0.wireOp",EDGE,"E17.filletArc"),sQuery(id+"F0.wireOp",EDGE,"E18.filletArc"),sQuery(id+"F0.wireOp",EDGE,"E19.filletArc"),sQuery(id+"F0.wireOp",EDGE,"E20.filletArc"),sQuery(id+"F0.wireOp",EDGE,"E25.0"),sQuery(id+"F0.wireOp",EDGE,"E25.1"),sQuery(id+"F0.wireOp",EDGE,"E25.2"),sQuery(id+"F0.wireOp",EDGE,"E25.3"),sQuery(id+"F0.wireOp",EDGE,"E25.4"),sQuery(id+"F0.wireOp",EDGE,"E25.5"),sQuery(id+"F0.wireOp",EDGE,"E25.6"),sQuery(id+"F0.wireOp",EDGE,"E25.7")])],"isStart":false});
            extrude(context, id + "F17", {"entities" : qUnion([Q0, Q1, Q2]), "endBound" : BoundingType.UP_TO_SURFACE, "depth" : 25 * mm, "endBoundEntityFace" : qUnion([Q3]), "offsetDistance" : 25 * mm});
        }
    });
